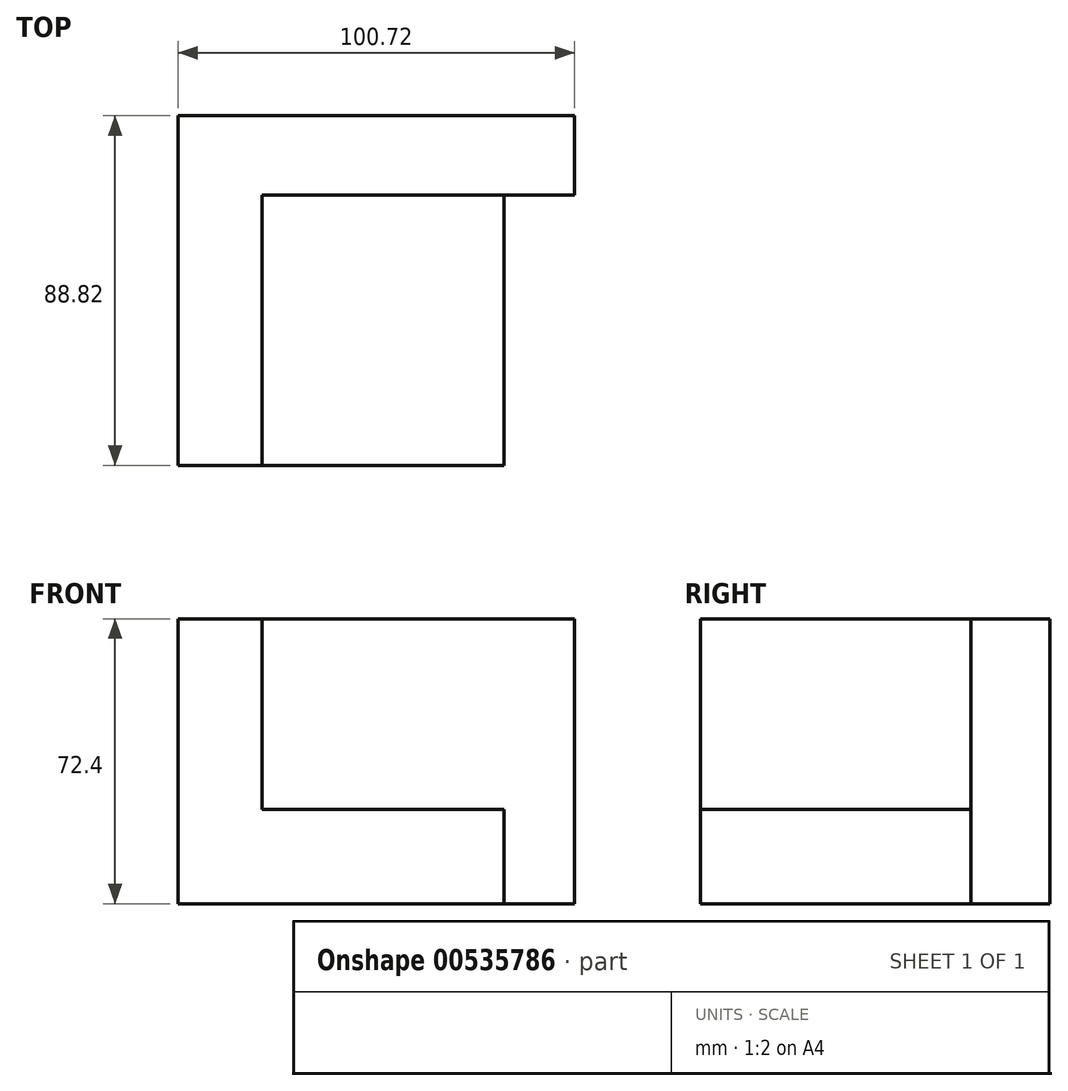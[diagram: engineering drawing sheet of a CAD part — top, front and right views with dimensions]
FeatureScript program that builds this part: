
annotation { "Feature Type Name" : "Feature", "Feature Type Description" : "" }
export const myFeature = defineFeature(function(context is Context, id is Id, definition is map)
    precondition{}
    {
        {
            var Q0;
            Q0=qCreatedBy(makeId("Top.planeOp"),FACE);
            var sketch = newSketch(context, id + "F0", { "sketchPlane" : qUnion([Q0])});
            skLineSegment(sketch, "E0.bottom", {"start": v(50.36, 44.41) * mm, "end": v(-50.36, 44.41) * mm});
            skLineSegment(sketch, "E0.top", {"start": v(-29.07, -44.41) * mm, "end": v(-50.36, -44.41) * mm});
            skLineSegment(sketch, "E0.left", {"start": v(50.36, 44.41) * mm, "end": v(50.36, 24.27) * mm});
            skLineSegment(sketch, "E0.right", {"start": v(-50.36, 44.41) * mm, "end": v(-50.36, -44.41) * mm});
            skPoint(sketch, "E0.middle", {"position": v(0, 0) * mm});
            skLineSegment(sketch, "E1.top", {"start": v(50.36, 24.27) * mm, "end": v(-29.07, 24.27) * mm});
            skLineSegment(sketch, "E1.right", {"start": v(-29.07, -44.41) * mm, "end": v(-29.07, 24.27) * mm});
            skSolve(sketch);
        }
        {
            var Q0;
            Q0=makeQuery(id+"F0.imprint","IMPRINT",FACE,{"disambiguationData":[TD([[makeQuery(id+"F0.imprint","IMPRINT",EDGE,{"derivedFrom":sQuery(id+"F0.wireOp",EDGE,"E0.bottom")}),1.0]])]});
            extrude(context, id + "F1", {"entities" : qUnion([Q0]), "endBound" : BoundingType.SYMMETRIC, "depth" : 72.4 * mm, "offsetDistance" : 25 * mm});
        }
        {
            var Q0;
            Q0=makeQuery(id+"F1.opExtrude","CAP_FACE",FACE,{"disambiguationData":[OSD([sQuery(id+"F0.wireOp",EDGE,"E0.bottom"),sQuery(id+"F0.wireOp",EDGE,"E0.top"),sQuery(id+"F0.wireOp",EDGE,"E0.left"),sQuery(id+"F0.wireOp",EDGE,"E0.right"),sQuery(id+"F0.wireOp",EDGE,"E1.top"),sQuery(id+"F0.wireOp",EDGE,"E1.right")])],"isStart":true});
            var sketch = newSketch(context, id + "F2", { "sketchPlane" : qUnion([Q0])});
            skLineSegment(sketch, "E2.bottom", {"start": v(-29.07, 44.41) * mm, "end": v(32.43, 44.41) * mm});
            skLineSegment(sketch, "E2.top", {"start": v(-29.07, -24.27) * mm, "end": v(32.43, -24.27) * mm});
            skLineSegment(sketch, "E2.left", {"start": v(-29.07, 44.41) * mm, "end": v(-29.07, -24.27) * mm});
            skLineSegment(sketch, "E2.right", {"start": v(32.43, 44.41) * mm, "end": v(32.43, -24.27) * mm});
            skSolve(sketch);
        }
        {
            var Q0;
            Q0=makeQuery(id+"F2.imprint","IMPRINT",FACE,{"disambiguationData":[TD([[makeQuery(id+"F2.imprint","IMPRINT",EDGE,{"derivedFrom":sQuery(id+"F2.wireOp",EDGE,"E2.bottom")}),-1.0]])]});
            extrude(context, id + "F3", {"entities" : qUnion([Q0]), "operationType" : NewBodyOperationType.ADD, "oppositeDirection" : true, "depth" : 24 * mm, "offsetDistance" : 25 * mm});
        }
    });
